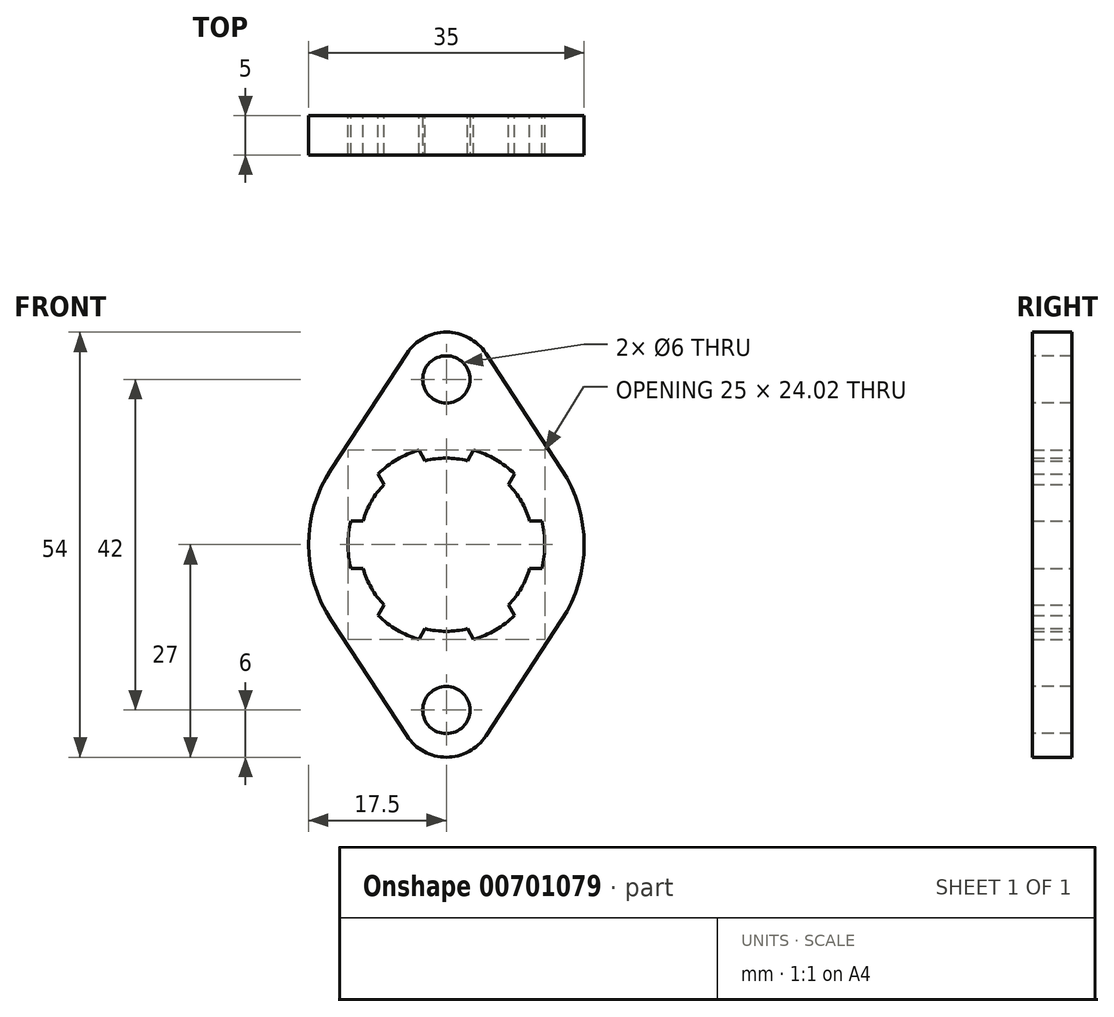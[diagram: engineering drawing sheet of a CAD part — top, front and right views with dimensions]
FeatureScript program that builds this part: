
annotation { "Feature Type Name" : "Feature", "Feature Type Description" : "" }
export const myFeature = defineFeature(function(context is Context, id is Id, definition is map)
    precondition{}
    {
        {
            var Q0;
            Q0=qCreatedBy(makeId("Front.planeOp"),FACE);
            var sketch = newSketch(context, id + "F0", { "sketchPlane" : qUnion([Q0])});
            skArc(sketch, "E0", {"start": v(-8.67, -9) * mm, "mid": v(-6.25, -10.83) * mm, "end": v(-3.47, -12) * mm});
            skArc(sketch, "E1", {"start": v(-10.58, -3) * mm, "mid": v(-9.53, -5.5) * mm, "end": v(-7.89, -7.67) * mm});
            skLineSegment(sketch, "E2", {"start": v(-20.16, 0) * mm, "end": v(25, 0) * mm, "construction": true});
            skLineSegment(sketch, "E3", {"start": v(-12.13, 3) * mm, "end": v(-10.58, 3) * mm});
            skLineSegment(sketch, "E4.MirrorCS", {"start": v(-12.13, -3) * mm, "end": v(-10.58, -3) * mm});
            skLineSegment(sketch, "E5.1.0", {"start": v(-3.47, -12) * mm, "end": v(-2.7, -10.67) * mm});
            skLineSegment(sketch, "E5.1.1", {"start": v(-8.67, -9) * mm, "end": v(-7.89, -7.67) * mm});
            skLineSegment(sketch, "E5.2.0", {"start": v(8.67, -9) * mm, "end": v(7.89, -7.67) * mm});
            skLineSegment(sketch, "E5.2.1", {"start": v(3.47, -12) * mm, "end": v(2.7, -10.67) * mm});
            skLineSegment(sketch, "E5.3.0", {"start": v(12.13, 3) * mm, "end": v(10.58, 3) * mm});
            skLineSegment(sketch, "E5.3.1", {"start": v(12.13, -3) * mm, "end": v(10.58, -3) * mm});
            skLineSegment(sketch, "E5.4.0", {"start": v(3.47, 12) * mm, "end": v(2.7, 10.67) * mm});
            skLineSegment(sketch, "E5.4.1", {"start": v(8.67, 9) * mm, "end": v(7.89, 7.67) * mm});
            skLineSegment(sketch, "E5.5.0", {"start": v(-8.67, 9) * mm, "end": v(-7.89, 7.67) * mm});
            skLineSegment(sketch, "E5.5.1", {"start": v(-3.47, 12) * mm, "end": v(-2.7, 10.67) * mm});
            skArc(sketch, "E6.trimOffspring", {"start": v(-7.89, 7.67) * mm, "mid": v(-9.53, 5.5) * mm, "end": v(-10.58, 3) * mm});
            skArc(sketch, "E7.trimOffspring", {"start": v(2.7, 10.67) * mm, "mid": v(0, 11) * mm, "end": v(-2.7, 10.67) * mm});
            skArc(sketch, "E8.trimOffspring", {"start": v(10.58, 3) * mm, "mid": v(9.53, 5.5) * mm, "end": v(7.89, 7.67) * mm});
            skArc(sketch, "E9.trimOffspring", {"start": v(7.89, -7.67) * mm, "mid": v(9.53, -5.5) * mm, "end": v(10.58, -3) * mm});
            skArc(sketch, "E10.trimOffspring", {"start": v(-2.7, -10.67) * mm, "mid": v(0, -11) * mm, "end": v(2.7, -10.67) * mm});
            skArc(sketch, "E11.trimOffspring", {"start": v(3.47, -12) * mm, "mid": v(6.25, -10.83) * mm, "end": v(8.67, -9) * mm});
            skArc(sketch, "E12.trimOffspring", {"start": v(12.13, -3) * mm, "mid": v(12.5, 0) * mm, "end": v(12.13, 3) * mm});
            skArc(sketch, "E13.trimOffspring", {"start": v(8.67, 9) * mm, "mid": v(6.25, 10.83) * mm, "end": v(3.47, 12) * mm});
            skArc(sketch, "E14.trimOffspring", {"start": v(-3.47, 12) * mm, "mid": v(-6.25, 10.83) * mm, "end": v(-8.67, 9) * mm});
            skArc(sketch, "E15.trimOffspring", {"start": v(-12.13, 3) * mm, "mid": v(-12.5, 0) * mm, "end": v(-12.13, -3) * mm});
            skCircle(sketch, "E16", {"center": v(0, 0) * mm, "radius": 17.5 * mm});
            skPoint(sketch, "E17", {"position": v(12.5, 0) * mm});
            skPoint(sketch, "E18", {"position": v(-12.5, 0) * mm});
            skPoint(sketch, "E19", {"position": v(0, 11) * mm});
            skPoint(sketch, "E20", {"position": v(0, -11) * mm});
            skSolve(sketch);
        }
        {
            var Q0;
            Q0 = qSketchRegion(id + "F0", true);
            extrude(context, id + "F1", {"entities" : qUnion([Q0]), "depth" : 5 * mm, "offsetDistance" : 25 * mm, "symmetric" : true});
        }
        {
            var Q0;
            Q0=makeQuery(id+"F1.opExtrude","CAP_FACE",FACE,{"disambiguationData":[OSD([sQuery(id+"F0.wireOp",EDGE,"E0"),sQuery(id+"F0.wireOp",EDGE,"E1"),sQuery(id+"F0.wireOp",EDGE,"E3"),sQuery(id+"F0.wireOp",EDGE,"E4.MirrorCS"),sQuery(id+"F0.wireOp",EDGE,"E5.1.0"),sQuery(id+"F0.wireOp",EDGE,"E5.1.1"),sQuery(id+"F0.wireOp",EDGE,"E5.2.0"),sQuery(id+"F0.wireOp",EDGE,"E5.2.1"),sQuery(id+"F0.wireOp",EDGE,"E5.3.0"),sQuery(id+"F0.wireOp",EDGE,"E5.3.1"),sQuery(id+"F0.wireOp",EDGE,"E5.4.0"),sQuery(id+"F0.wireOp",EDGE,"E5.4.1"),sQuery(id+"F0.wireOp",EDGE,"E5.5.0"),sQuery(id+"F0.wireOp",EDGE,"E5.5.1"),sQuery(id+"F0.wireOp",EDGE,"E6.trimOffspring"),sQuery(id+"F0.wireOp",EDGE,"E7.trimOffspring"),sQuery(id+"F0.wireOp",EDGE,"E8.trimOffspring"),sQuery(id+"F0.wireOp",EDGE,"E9.trimOffspring"),sQuery(id+"F0.wireOp",EDGE,"E10.trimOffspring"),sQuery(id+"F0.wireOp",EDGE,"E11.trimOffspring"),sQuery(id+"F0.wireOp",EDGE,"E12.trimOffspring"),sQuery(id+"F0.wireOp",EDGE,"E13.trimOffspring"),sQuery(id+"F0.wireOp",EDGE,"E14.trimOffspring"),sQuery(id+"F0.wireOp",EDGE,"E15.trimOffspring"),sQuery(id+"F0.wireOp",EDGE,"E16")])],"isStart":false});
            var sketch = newSketch(context, id + "F2", { "sketchPlane" : qUnion([Q0])});
            skLineSegment(sketch, "E21", {"start": v(-14.64, 9.58) * mm, "end": v(-5.02, 24.29) * mm});
            skArc(sketch, "E22", {"start": v(-5.02, 24.29) * mm, "mid": v(0, 27) * mm, "end": v(5.02, 24.29) * mm});
            skLineSegment(sketch, "E23", {"start": v(0, -21) * mm, "end": v(0, 21) * mm, "construction": true});
            skLineSegment(sketch, "E24.MirrorCS", {"start": v(14.64, 9.58) * mm, "end": v(5.02, 24.29) * mm});
            skLineSegment(sketch, "E25", {"start": v(-23.99, 0) * mm, "end": v(39.38, 0) * mm, "construction": true});
            skPoint(sketch, "E25.startSnap0", {"position": v(0, 0) * mm});
            skLineSegment(sketch, "E26.MirrorCS", {"start": v(-14.64, -9.58) * mm, "end": v(-5.02, -24.29) * mm});
            skArc(sketch, "E27.MirrorCS", {"start": v(-5.02, -24.29) * mm, "mid": v(0, -27) * mm, "end": v(5.02, -24.29) * mm});
            skLineSegment(sketch, "E28.MirrorCS", {"start": v(14.64, -9.58) * mm, "end": v(5.02, -24.29) * mm});
            skCircle(sketch, "E29", {"center": v(0, 21) * mm, "radius": 3 * mm});
            skCircle(sketch, "E30", {"center": v(0, -21) * mm, "radius": 3 * mm});
            skArc(sketch, "E31.0", {"start": v(-14.64, -9.58) * mm, "mid": v(0, -17.5) * mm, "end": v(14.64, -9.58) * mm});
            skArc(sketch, "E32.trimOffspring", {"start": v(14.64, 9.58) * mm, "mid": v(0, 17.5) * mm, "end": v(-14.64, 9.58) * mm});
            skSolve(sketch);
        }
        {
            var Q0;
            Q0 = qSketchRegion(id + "F2", true);
            var Q1;
            Q1=makeQuery(id+"F1.opExtrude","CAP_FACE",FACE,{"disambiguationData":[OSD([sQuery(id+"F0.wireOp",EDGE,"E0"),sQuery(id+"F0.wireOp",EDGE,"E1"),sQuery(id+"F0.wireOp",EDGE,"E3"),sQuery(id+"F0.wireOp",EDGE,"E4.MirrorCS"),sQuery(id+"F0.wireOp",EDGE,"E5.1.0"),sQuery(id+"F0.wireOp",EDGE,"E5.1.1"),sQuery(id+"F0.wireOp",EDGE,"E5.2.0"),sQuery(id+"F0.wireOp",EDGE,"E5.2.1"),sQuery(id+"F0.wireOp",EDGE,"E5.3.0"),sQuery(id+"F0.wireOp",EDGE,"E5.3.1"),sQuery(id+"F0.wireOp",EDGE,"E5.4.0"),sQuery(id+"F0.wireOp",EDGE,"E5.4.1"),sQuery(id+"F0.wireOp",EDGE,"E5.5.0"),sQuery(id+"F0.wireOp",EDGE,"E5.5.1"),sQuery(id+"F0.wireOp",EDGE,"E6.trimOffspring"),sQuery(id+"F0.wireOp",EDGE,"E7.trimOffspring"),sQuery(id+"F0.wireOp",EDGE,"E8.trimOffspring"),sQuery(id+"F0.wireOp",EDGE,"E9.trimOffspring"),sQuery(id+"F0.wireOp",EDGE,"E10.trimOffspring"),sQuery(id+"F0.wireOp",EDGE,"E11.trimOffspring"),sQuery(id+"F0.wireOp",EDGE,"E12.trimOffspring"),sQuery(id+"F0.wireOp",EDGE,"E13.trimOffspring"),sQuery(id+"F0.wireOp",EDGE,"E14.trimOffspring"),sQuery(id+"F0.wireOp",EDGE,"E15.trimOffspring"),sQuery(id+"F0.wireOp",EDGE,"E16")])],"isStart":true});
            extrude(context, id + "F3", {"entities" : qUnion([Q0]), "operationType" : NewBodyOperationType.ADD, "endBound" : BoundingType.UP_TO_SURFACE, "oppositeDirection" : true, "depth" : 25 * mm, "endBoundEntityFace" : qUnion([Q1]), "offsetDistance" : 25 * mm});
        }
    });
